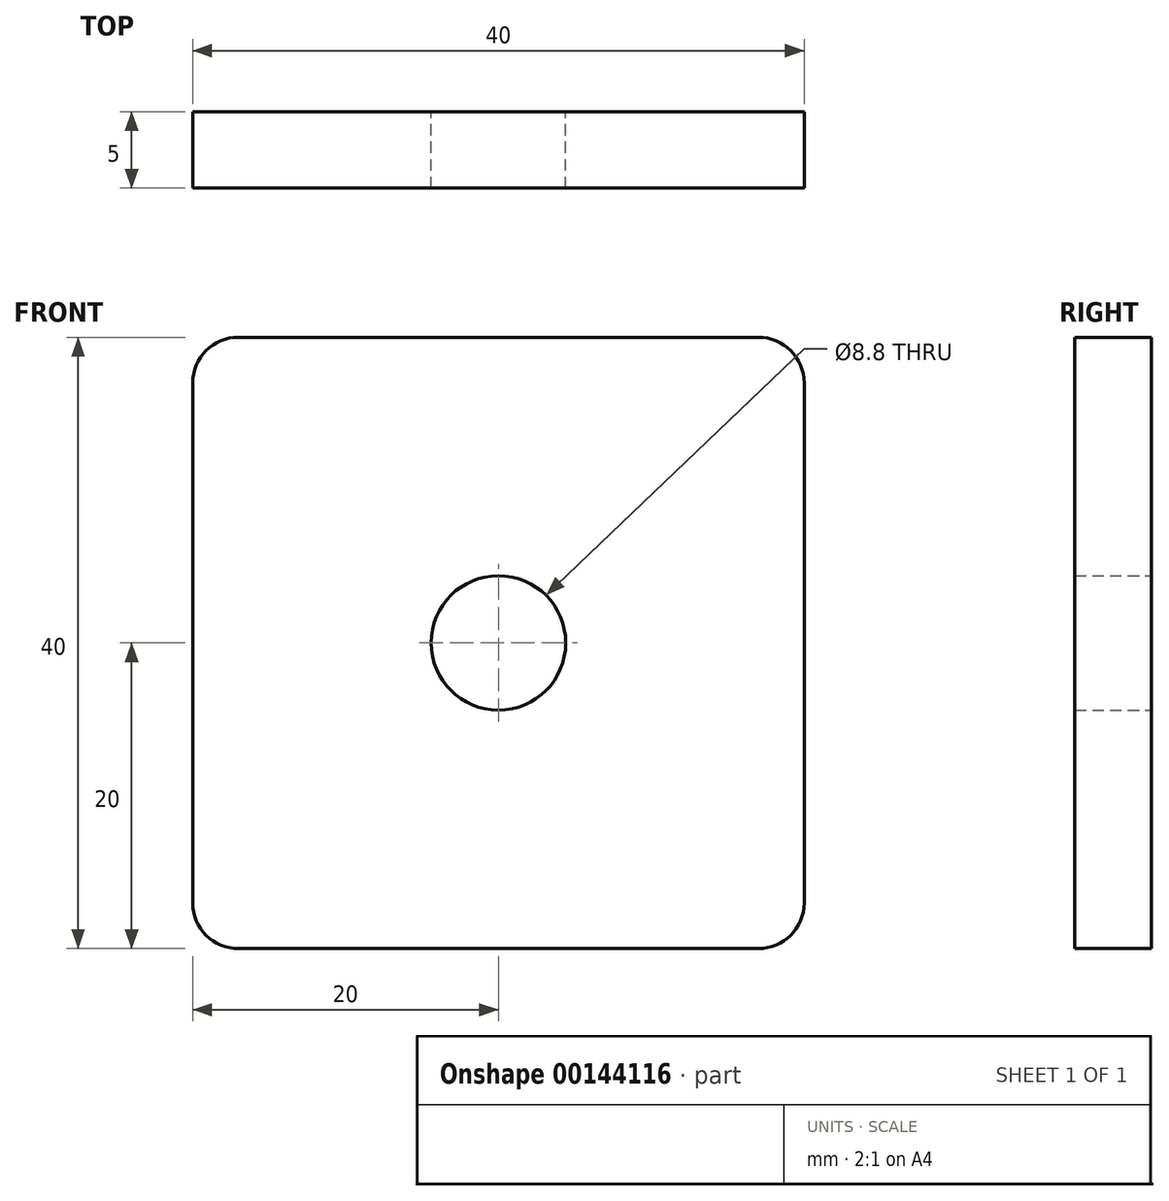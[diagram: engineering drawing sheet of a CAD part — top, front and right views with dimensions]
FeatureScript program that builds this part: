
annotation { "Feature Type Name" : "Feature", "Feature Type Description" : "" }
export const myFeature = defineFeature(function(context is Context, id is Id, definition is map)
    precondition{}
    {
        {
            var Q0;
            Q0=qCreatedBy(makeId("Front.planeOp"),FACE);
            var sketch = newSketch(context, id + "F0", { "sketchPlane" : qUnion([Q0])});
            skLineSegment(sketch, "E0.bottom", {"start": v(17, 20) * mm, "end": v(-17, 20) * mm});
            skLineSegment(sketch, "E0.top", {"start": v(17, -20) * mm, "end": v(-17, -20) * mm});
            skLineSegment(sketch, "E0.left", {"start": v(20, 17) * mm, "end": v(20, -17) * mm});
            skLineSegment(sketch, "E0.right", {"start": v(-20, 17) * mm, "end": v(-20, -17) * mm});
            skPoint(sketch, "E0.middle", {"position": v(0, 0) * mm});
            skPoint(sketch, "E1.visualSharp", {"position": v(-20, 20) * mm});
            skArc(sketch, "E1.filletArc", {"start": v(-17, 20) * mm, "mid": v(-19.12, 19.12) * mm, "end": v(-20, 17) * mm});
            skPoint(sketch, "E2.visualSharp", {"position": v(20, 20) * mm});
            skArc(sketch, "E2.filletArc", {"start": v(20, 17) * mm, "mid": v(19.12, 19.12) * mm, "end": v(17, 20) * mm});
            skPoint(sketch, "E3.visualSharp", {"position": v(20, -20) * mm});
            skArc(sketch, "E3.filletArc", {"start": v(17, -20) * mm, "mid": v(19.12, -19.12) * mm, "end": v(20, -17) * mm});
            skPoint(sketch, "E4.visualSharp", {"position": v(-20, -20) * mm});
            skArc(sketch, "E4.filletArc", {"start": v(-20, -17) * mm, "mid": v(-19.12, -19.12) * mm, "end": v(-17, -20) * mm});
            skSolve(sketch);
        }
        {
            var Q0;
            Q0=makeQuery(id+"F0.imprint","IMPRINT",FACE,{"disambiguationData":[TD([[makeQuery(id+"F0.imprint","IMPRINT",EDGE,{"derivedFrom":sQuery(id+"F0.wireOp",EDGE,"E0.bottom")}),1.0]])]});
            extrude(context, id + "F1", {"entities" : qUnion([Q0]), "depth" : 5 * mm});
        }
        {
            var Q0;
            Q0=makeQuery(id+"F1.opExtrude","CAP_FACE",FACE,{"disambiguationData":[OSD([sQuery(id+"F0.wireOp",EDGE,"E0.bottom"),sQuery(id+"F0.wireOp",EDGE,"E0.top"),sQuery(id+"F0.wireOp",EDGE,"E0.left"),sQuery(id+"F0.wireOp",EDGE,"E0.right"),sQuery(id+"F0.wireOp",EDGE,"E1.filletArc"),sQuery(id+"F0.wireOp",EDGE,"E2.filletArc"),sQuery(id+"F0.wireOp",EDGE,"E3.filletArc"),sQuery(id+"F0.wireOp",EDGE,"E4.filletArc")])],"isStart":false});
            var sketch = newSketch(context, id + "F2", { "sketchPlane" : qUnion([Q0])});
            skPoint(sketch, "E5", {"position": v(0, 0) * mm});
            skSolve(sketch);
        }
        {
            var Q0;
            Q0=sQuery(id+"F2.wireOp",VERTEX,"E5");
            var Q1;
            Q1=makeQuery(id+"F1.opExtrude","SWEPT_BODY",BODY,{"disambiguationData":[OSD([sQuery(id+"F0.wireOp",EDGE,"E0.bottom"),sQuery(id+"F0.wireOp",EDGE,"E0.top"),sQuery(id+"F0.wireOp",EDGE,"E0.left"),sQuery(id+"F0.wireOp",EDGE,"E0.right"),sQuery(id+"F0.wireOp",EDGE,"E1.filletArc"),sQuery(id+"F0.wireOp",EDGE,"E2.filletArc"),sQuery(id+"F0.wireOp",EDGE,"E3.filletArc"),sQuery(id+"F0.wireOp",EDGE,"E4.filletArc")])]});
            hole(context, id + "F3", {"style" : HoleStyle.SIMPLE, "endStyle" : HoleEndStyle.THROUGH, "standardTappedOrClearance" : lookupTablePath({ "standard" : "ISO", "engagement" : "75%", "pitch" : "1.25 mm", "size" : "M10", "type" : "Tapped" }), "standardBlindInLast" : lookupTablePath({ "standard" : "ISO", "engagement" : "75%", "pitch" : "1.25 mm", "size" : "M10", "type" : "Tapped" }), "holeDiameter" : 8.8 * mm, "locations" : qUnion([Q0]), "scope" : qUnion([Q1]), "isTappedThrough" : true, "majorDiameter" : 10 * mm, "showTappedDepth" : true, "startStyle" : HoleStartStyle.PART});
        }
    });
